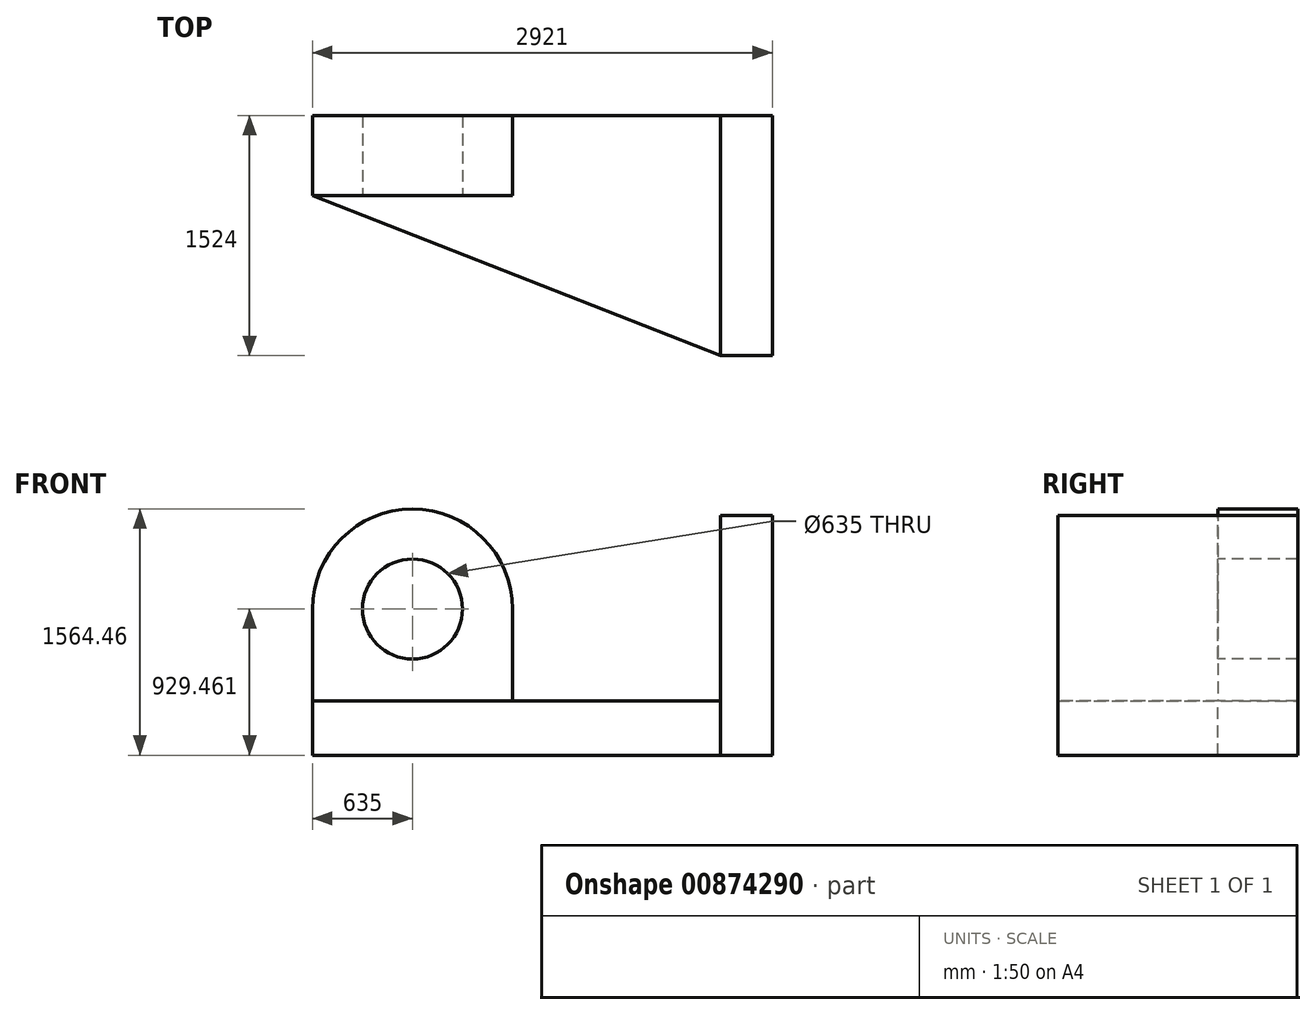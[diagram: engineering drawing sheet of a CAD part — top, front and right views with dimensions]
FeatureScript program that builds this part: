
annotation { "Feature Type Name" : "Feature", "Feature Type Description" : "" }
export const myFeature = defineFeature(function(context is Context, id is Id, definition is map)
    precondition{}
    {
        {
            var Q0;
            Q0=qCreatedBy(makeId("Right.planeOp"),FACE);
            var sketch = newSketch(context, id + "F0", { "sketchPlane" : qUnion([Q0])});
            skLineSegment(sketch, "E0.bottom", {"start": v(0, 0) * mm, "end": v(-1524, 0) * mm});
            skLineSegment(sketch, "E0.top", {"start": v(0, 1524) * mm, "end": v(-1524, 1524) * mm});
            skLineSegment(sketch, "E0.left", {"start": v(0, 0) * mm, "end": v(0, 1524) * mm});
            skLineSegment(sketch, "E0.right", {"start": v(-1524, 0) * mm, "end": v(-1524, 1524) * mm});
            skSolve(sketch);
        }
        {
            var Q0;
            Q0=makeQuery(id+"F0.imprint","IMPRINT",FACE,{"disambiguationData":[TD([[makeQuery(id+"F0.imprint","IMPRINT",EDGE,{"derivedFrom":sQuery(id+"F0.wireOp",EDGE,"E0.bottom")}),-1.0]])]});
            extrude(context, id + "F1", {"entities" : qUnion([Q0]), "depth" : 25.4 * mm, "offsetDistance" : 25.4 * mm});
        }
        {
            var Q0;
            Q0=makeQuery(id+"F1.opExtrude","CAP_FACE",FACE,{"disambiguationData":[OSD([sQuery(id+"F0.wireOp",EDGE,"E0.bottom"),sQuery(id+"F0.wireOp",EDGE,"E0.top"),sQuery(id+"F0.wireOp",EDGE,"E0.left"),sQuery(id+"F0.wireOp",EDGE,"E0.right")])],"isStart":false});
            extrude(context, id + "F2", {"entities" : qUnion([Q0]), "operationType" : NewBodyOperationType.ADD, "depth" : 304.8 * mm, "offsetDistance" : 25.4 * mm});
        }
        {
            var Q0;
            Q0=makeQuery(id+"F2.opExtrude","CAP_FACE",FACE,{"disambiguationData":[OSD([sQuery(id+"F0.wireOp",EDGE,"E0.bottom"),sQuery(id+"F0.wireOp",EDGE,"E0.top"),sQuery(id+"F0.wireOp",EDGE,"E0.left"),sQuery(id+"F0.wireOp",EDGE,"E0.right")])],"isStart":false});
            var sketch = newSketch(context, id + "F3", { "sketchPlane" : qUnion([Q0])});
            skLineSegment(sketch, "E1.bottom", {"start": v(-1524, 0) * mm, "end": v(0, 0) * mm});
            skLineSegment(sketch, "E1.top", {"start": v(-1524, 345.26) * mm, "end": v(0, 345.26) * mm});
            skLineSegment(sketch, "E1.left", {"start": v(-1524, 0) * mm, "end": v(-1524, 345.26) * mm});
            skLineSegment(sketch, "E1.right", {"start": v(0, 0) * mm, "end": v(0, 345.26) * mm});
            skSolve(sketch);
        }
        {
            var Q0;
            Q0=makeQuery(id+"F3.imprint","IMPRINT",FACE,{"disambiguationData":[TD([[makeQuery(id+"F3.imprint","IMPRINT",EDGE,{"derivedFrom":sQuery(id+"F3.wireOp",EDGE,"E1.bottom")}),-1.0]])]});
            var Q1;
            Q1=sQuery(id+"F3.wireOp",EDGE,"E1.top");
            extrude(context, id + "F4", {"entities" : qUnion([Q0]), "operationType" : NewBodyOperationType.ADD, "surfaceEntities" : qUnion([Q1]), "oppositeDirection" : true, "depth" : 2921 * mm, "offsetDistance" : 25.4 * mm});
        }
        {
            var Q0;
            Q0=makeQuery(id+"F4.opExtrude","SWEPT_FACE",FACE,{"disambiguationData":[OSD([sQuery(id+"F3.wireOp",EDGE,"E1.top")])]});
            var sketch = newSketch(context, id + "F5", { "sketchPlane" : qUnion([Q0])});
            skLineSegment(sketch, "E2.bottom", {"start": v(-2590.8, 0) * mm, "end": v(-1320.8, 0) * mm});
            skLineSegment(sketch, "E2.top", {"start": v(-2590.8, -508) * mm, "end": v(-1320.8, -508) * mm});
            skLineSegment(sketch, "E2.left", {"start": v(-2590.8, 0) * mm, "end": v(-2590.8, -508) * mm});
            skLineSegment(sketch, "E2.right", {"start": v(-1320.8, 0) * mm, "end": v(-1320.8, -508) * mm});
            skSolve(sketch);
        }
        {
            var Q0;
            Q0=makeQuery(id+"F5.imprint","IMPRINT",FACE,{"disambiguationData":[TD([[makeQuery(id+"F5.imprint","IMPRINT",EDGE,{"derivedFrom":sQuery(id+"F5.wireOp",EDGE,"E2.bottom")}),-1.0]])]});
            extrude(context, id + "F6", {"entities" : qUnion([Q0]), "operationType" : NewBodyOperationType.ADD, "depth" : 584.2 * mm, "offsetDistance" : 25.4 * mm});
        }
        {
            var Q0;
            Q0=makeQuery(id+"F6.opExtrude","SWEPT_FACE",FACE,{"disambiguationData":[OSD([sQuery(id+"F5.wireOp",EDGE,"E2.top")])]});
            var sketch = newSketch(context, id + "F7", { "sketchPlane" : qUnion([Q0])});
            skCircle(sketch, "E3", {"center": v(-1955.8, 929.46) * mm, "radius": 635 * mm});
            skSolve(sketch);
        }
        {
            var Q0;
            {var subQ1=sQuery(id+"F5.wireOp",EDGE,"E2.top");var subQ2=makeQuery(id+"F6.opExtrude","CAP_EDGE",EDGE,{"disambiguationData":[OSD([subQ1])],"isStart":false});Q0=makeQuery(id+"F7.imprint","IMPRINT",FACE,{"disambiguationData":[TD([[makeQuery(id+"F7.imprint","IMPRINT",EDGE,{"derivedFrom":subQ2}),1.0]])]});}
            extrude(context, id + "F8", {"entities" : qUnion([Q0]), "operationType" : NewBodyOperationType.ADD, "oppositeDirection" : true, "depth" : 508 * mm, "offsetDistance" : 25.4 * mm});
        }
        {
            var Q0;
            {var subQ0=sQuery(id+"F5.wireOp",EDGE,"E2.top");Q0=makeQuery(id+"F8.boolean.opBoolean","MERGE",FACE,{"derivedFrom":[makeQuery(id+"F6.opExtrude","SWEPT_FACE",FACE,{"disambiguationData":[OSD([subQ0])]}),makeQuery(id+"F8.opExtrude","CAP_FACE",FACE,{"disambiguationData":[OSD([subQ0,sQuery(id+"F7.wireOp",EDGE,"E3")])],"isStart":true})]});}
            var sketch = newSketch(context, id + "F9", { "sketchPlane" : qUnion([Q0])});
            skCircle(sketch, "E4", {"center": v(-1955.8, 929.46) * mm, "radius": 317.5 * mm});
            skSolve(sketch);
        }
        {
            var Q0;
            Q0=makeQuery(id+"F9.imprint","IMPRINT",FACE,{"disambiguationData":[TD([[makeQuery(id+"F9.imprint","IMPRINT",EDGE,{"derivedFrom":sQuery(id+"F9.wireOp",EDGE,"E4")}),1.0]])]});
            extrude(context, id + "F10", {"entities" : qUnion([Q0]), "operationType" : NewBodyOperationType.REMOVE, "oppositeDirection" : true, "depth" : 5212.08 * mm, "offsetDistance" : 25.4 * mm});
        }
        {
            var Q0;
            Q0=makeQuery(id+"F4.opExtrude","SWEPT_FACE",FACE,{"disambiguationData":[OSD([sQuery(id+"F3.wireOp",EDGE,"E1.top")])]});
            var sketch = newSketch(context, id + "F11", { "sketchPlane" : qUnion([Q0])});
            skLineSegment(sketch, "E5", {"start": v(-2590.8, -508) * mm, "end": v(0, -1524) * mm});
            skLineSegment(sketch, "E6", {"start": v(0, -1524) * mm, "end": v(-2590.8, -1524) * mm});
            skLineSegment(sketch, "E7", {"start": v(-2590.8, -1524) * mm, "end": v(-2590.8, -508) * mm});
            skSolve(sketch);
        }
        {
            var Q0;
            Q0=makeQuery(id+"F11.imprint","IMPRINT",FACE,{"disambiguationData":[TD([[makeQuery(id+"F11.imprint","IMPRINT",EDGE,{"derivedFrom":sQuery(id+"F11.wireOp",EDGE,"E5")}),-1.0]])]});
            extrude(context, id + "F12", {"entities" : qUnion([Q0]), "operationType" : NewBodyOperationType.REMOVE, "oppositeDirection" : true, "depth" : 508 * mm, "offsetDistance" : 25.4 * mm});
        }
    });
